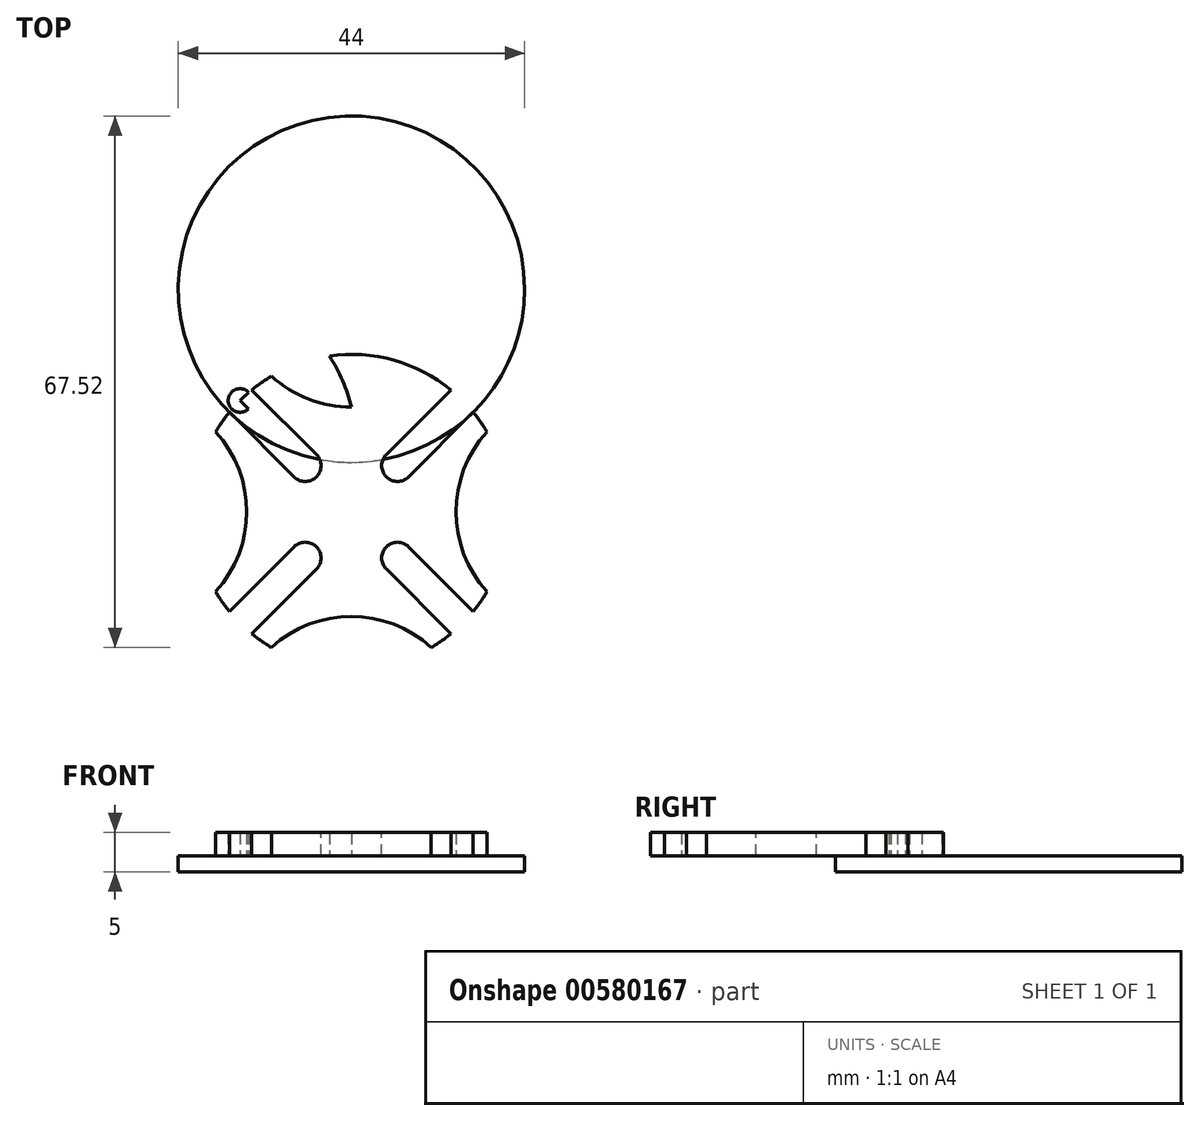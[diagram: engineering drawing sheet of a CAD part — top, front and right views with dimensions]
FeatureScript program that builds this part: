
annotation { "Feature Type Name" : "Feature", "Feature Type Description" : "" }
export const myFeature = defineFeature(function(context is Context, id is Id, definition is map)
    precondition{}
    {
        {
            var Q0;
            Q0=qCreatedBy(makeId("Top.planeOp"),FACE);
            var sketch = newSketch(context, id + "F0", { "sketchPlane" : qUnion([Q0])});
            skCircle(sketch, "E0", {"center": v(0, 28.28) * mm, "radius": 15 * mm});
            skCircle(sketch, "E1", {"center": v(0, 0) * mm, "radius": 20 * mm});
            skCircle(sketch, "E2", {"center": v(0, 28.28) * mm, "radius": 22 * mm});
            skLineSegment(sketch, "E3", {"start": v(0, 0) * mm, "end": v(-27.83, 27.83) * mm, "construction": true});
            skLineSegment(sketch, "E4", {"start": v(0, 0) * mm, "end": v(0, 50.85) * mm, "construction": true});
            skLineSegment(sketch, "E5.MirrorCS", {"start": v(0, 0) * mm, "end": v(27.83, 27.83) * mm, "construction": true});
            skCircle(sketch, "E6", {"center": v(0, 28.28) * mm, "radius": 20 * mm, "construction": true});
            skLineSegment(sketch, "E7", {"start": v(-14.14, 14.14) * mm, "end": v(0, 0) * mm, "construction": true});
            skLineSegment(sketch, "E8", {"start": v(-5.86, 3.03) * mm, "end": v(-15.49, 12.66) * mm});
            skCircle(sketch, "E9", {"center": v(-14.14, 14.14) * mm, "radius": 1.5 * mm});
            skLineSegment(sketch, "E10.MirrorCS", {"start": v(-3.03, 5.86) * mm, "end": v(-12.66, 15.49) * mm});
            skLineSegment(sketch, "E11", {"start": v(-5.86, 3.03) * mm, "end": v(-3.03, 5.86) * mm});
            skLineSegment(sketch, "E12", {"start": v(0, 0) * mm, "end": v(-14.14, 14.14) * mm});
            skLineSegment(sketch, "E13.MirrorCS", {"start": v(0, 0) * mm, "end": v(14.14, 14.14) * mm});
            skLineSegment(sketch, "E14.MirrorCS", {"start": v(3.03, 5.86) * mm, "end": v(12.66, 15.49) * mm});
            skLineSegment(sketch, "E15.MirrorCS", {"start": v(5.86, 3.03) * mm, "end": v(15.49, 12.66) * mm});
            skLineSegment(sketch, "E16.MirrorCS", {"start": v(5.86, 3.03) * mm, "end": v(3.03, 5.86) * mm});
            skCircle(sketch, "E17", {"center": v(0, 0) * mm, "radius": 8.28 * mm, "construction": true});
            skLineSegment(sketch, "E18", {"start": v(0, 28.28) * mm, "end": v(-14.14, 14.14) * mm, "construction": true});
            skLineSegment(sketch, "E19", {"start": v(0, 28.28) * mm, "end": v(-16.62, 28.28) * mm, "construction": true});
            skArc(sketch, "E20", {"start": v(0, 13.28) * mm, "mid": v(-5.35, 22.94) * mm, "end": v(-15, 28.28) * mm});
            skSolve(sketch);
        }
        {
            var Q0;
            {var subQ1=sQuery(id+"F0.wireOp",EDGE,"E1");var subQ3=sQuery(id+"F0.wireOp",EDGE,"E0");var subQ4=makeQuery(id+"F0.imprint","INTERSECT",VERTEX,{"disambiguationData":[OD(0.0)],"derivedFrom":[subQ3,subQ1]});Q0=makeQuery(id+"F0.imprint","IMPRINT",FACE,{"disambiguationData":[TD([[makeQuery(id+"F0.imprint","IMPRINT",EDGE,{"disambiguationData":[TD([[subQ4,-1.0]])],"derivedFrom":subQ3}),-1.0]])]});}
            var Q1;
            {var subQ5=sQuery(id+"F0.wireOp",EDGE,"E10.MirrorCS");var subQ11=sQuery(id+"F0.wireOp",EDGE,"E2");var subQ12=makeQuery(id+"F0.imprint","INTERSECT",VERTEX,{"derivedFrom":[subQ11,subQ5]});Q1=makeQuery(id+"F0.imprint","IMPRINT",FACE,{"disambiguationData":[TD([[makeQuery(id+"F0.imprint","IMPRINT",EDGE,{"disambiguationData":[TD([[subQ12,-1.0]])],"derivedFrom":subQ11}),-1.0]])]});}
            extrude(context, id + "F1", {"entities" : qUnion([Q0, Q1]), "depth" : 3 * mm, "offsetDistance" : 25 * mm});
        }
        {
            var Q0;
            Q0=makeQuery(id+"F1.opExtrude","SWEPT_EDGE",EDGE,{"disambiguationData":[OSD([sQuery(id+"F0.wireOp",EDGE,"E10.MirrorCS"),sQuery(id+"F0.wireOp",EDGE,"E11")])]});
            var Q1;
            Q1=makeQuery(id+"F1.opExtrude","SWEPT_EDGE",EDGE,{"disambiguationData":[OSD([sQuery(id+"F0.wireOp",EDGE,"E14.MirrorCS"),sQuery(id+"F0.wireOp",EDGE,"E16.MirrorCS")])]});
            fillet(context, id + "F2", {"entities" : qUnion([Q0, Q1]), "tangentPropagation" : true, "radius" : 2 * mm, "defaultsChanged" : true, "vertexSettings" : [], "allowEdgeOverflow" : false});
        }
        {
            var Q0;
            Q0=makeQuery(id+"F1.opExtrude","SWEPT_BODY",BODY,{"disambiguationData":[OSD([sQuery(id+"F0.wireOp",EDGE,"GwWt0gKQ-UlIg-HZDy-arK7-RWpiHWEL3f2j"),sQuery(id+"F0.wireOp",EDGE,"E0"),sQuery(id+"F0.wireOp",EDGE,"E1"),sQuery(id+"F0.wireOp",EDGE,"E2"),sQuery(id+"F0.wireOp",EDGE,"E8"),sQuery(id+"F0.wireOp",EDGE,"E10.MirrorCS"),sQuery(id+"F0.wireOp",EDGE,"E11"),sQuery(id+"F0.wireOp",EDGE,"E12"),sQuery(id+"F0.wireOp",EDGE,"E13.MirrorCS"),sQuery(id+"F0.wireOp",EDGE,"E14.MirrorCS"),sQuery(id+"F0.wireOp",EDGE,"E15.MirrorCS"),sQuery(id+"F0.wireOp",EDGE,"E16.MirrorCS")])]});
            var Q1;
            Q1=makeQuery(id+"F1.opExtrude","SWEPT_EDGE",EDGE,{"disambiguationData":[OSD([sQuery(id+"F0.wireOp",EDGE,"E12"),sQuery(id+"F0.wireOp",EDGE,"E13.MirrorCS")])]});
            circularPattern(context, id + "F3", {"operationType" : NewBodyOperationType.ADD, "entities" : qUnion([Q0]), "axis" : qUnion([Q1]), "angle" : 360 * degree, "instanceCount" : 4, "equalSpace" : true});
        }
        {
            var Q0;
            {var subQ1=sQuery(id+"F0.wireOp",EDGE,"E0");var subQ3=makeQuery(id+"F0.imprint","IMPRINT",VERTEX,{"derivedFrom":subQ1});Q0=makeQuery(id+"F0.imprint","IMPRINT",FACE,{"disambiguationData":[TD([[makeQuery(id+"F0.imprint","IMPRINT",EDGE,{"disambiguationData":[TD([[subQ3,-1.0]])],"derivedFrom":subQ1}),1.0]])]});}
            var Q1;
            {var subQ0=sQuery(id+"F0.wireOp",EDGE,"E20");var subQ1=sQuery(id+"F0.wireOp",EDGE,"E0");var subQ2=makeQuery(id+"F0.imprint","INTERSECT",VERTEX,{"disambiguationData":[OD(0.0)],"derivedFrom":[subQ1,subQ0]});Q1=makeQuery(id+"F0.imprint","IMPRINT",FACE,{"disambiguationData":[TD([[makeQuery(id+"F0.imprint","IMPRINT",EDGE,{"disambiguationData":[TD([[subQ2,-1.0]])],"derivedFrom":subQ1}),1.0]])]});}
            extrude(context, id + "F4", {"entities" : qUnion([Q0, Q1]), "depth" : 3 * mm, "offsetDistance" : 25 * mm});
        }
        {
            var Q0;
            Q0=qCreatedBy(makeId("Top.planeOp"),FACE);
            var sketch = newSketch(context, id + "F5", { "sketchPlane" : qUnion([Q0])});
            skCircle(sketch, "E21", {"center": v(0, 28.28) * mm, "radius": 22 * mm});
            skSolve(sketch);
        }
        {
            var Q0;
            Q0 = qSketchRegion(id + "F5", true);
            extrude(context, id + "F6", {"entities" : qUnion([Q0]), "operationType" : NewBodyOperationType.ADD, "oppositeDirection" : true, "depth" : 2 * mm, "offsetDistance" : 25 * mm});
        }
        {
            var Q0;
            {var subQ0=sQuery(id+"F0.wireOp",EDGE,"E1");var subQ1=makeQuery(id+"F0.imprint","INTERSECT",VERTEX,{"derivedFrom":[subQ0,sQuery(id+"F0.wireOp",EDGE,"E12")]});Q0=makeQuery(id+"F0.imprint","IMPRINT",FACE,{"disambiguationData":[TD([[makeQuery(id+"F0.imprint","IMPRINT",EDGE,{"disambiguationData":[TD([[subQ1,1.0]])],"derivedFrom":subQ0}),-1.0]])]});}
            var Q1;
            {var subQ3=sQuery(id+"F0.wireOp",EDGE,"E9");var subQ5=makeQuery(id+"F0.imprint","IMPRINT",VERTEX,{"derivedFrom":subQ3});Q1=makeQuery(id+"F0.imprint","IMPRINT",FACE,{"disambiguationData":[TD([[makeQuery(id+"F0.imprint","IMPRINT",EDGE,{"disambiguationData":[TD([[subQ5,-1.0]])],"derivedFrom":subQ3}),1.0]])]});}
            var Q2;
            {var subQ0=sQuery(id+"F0.wireOp",EDGE,"E12");var subQ1=sQuery(id+"F0.wireOp",EDGE,"E1");var subQ2=makeQuery(id+"F0.imprint","INTERSECT",VERTEX,{"derivedFrom":[subQ1,subQ0]});Q2=makeQuery(id+"F0.imprint","IMPRINT",FACE,{"disambiguationData":[TD([[makeQuery(id+"F0.imprint","IMPRINT",EDGE,{"disambiguationData":[TD([[subQ2,-1.0]])],"derivedFrom":subQ1}),1.0]])]});}
            extrude(context, id + "F7", {"entities" : qUnion([Q0, Q1, Q2]), "operationType" : NewBodyOperationType.ADD, "depth" : 3 * mm, "offsetDistance" : 25 * mm});
        }
    });
